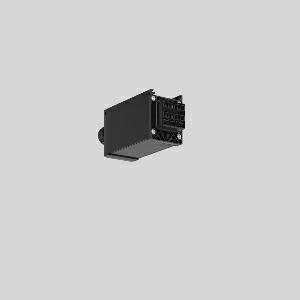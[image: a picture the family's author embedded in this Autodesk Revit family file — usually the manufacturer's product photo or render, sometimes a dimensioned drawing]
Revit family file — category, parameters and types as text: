
# Revit family: linedo_anfangseinspeisung_982859_003_1_55de
name_source: partatom
category: Lighting Fixtures
units: mm (PartAtom-declared; Revit-internal decimal feet)

## family parameters
Cut with Voids When Loaded = No
Host = Face
Light Source = No
Part Type = Normal
Room Calculation Point = No
Round Connector Dimension = Use Diameter
Shared = No

## types (1)
- LINEDO Anfangseinspeisung
    Apparent Load = 0 VA
    Default Elevation = 1800 mm
    Description = Series: LINEDO
Initial power feed (short Version), 7-pole, connection plug. Housing: extruded aluminium profile, powder-coated. Cover made of plastic, surface like housing. LINEDO plug system, plastic, black. 1 cable gland (M25). Cable gland on side or on top. Convenient connection with flat connector.
Colour: black
Length: 152 mm
Width: 58 mm
Height: 76 mm
Weight: 283 g
    Height = 76 mm
    Lamp = 0 x
    Length = 152 mm
    Luminous efficacy = 0 lm/W
    Manufacturer = RZB
    ModVariant = No
    Model = 982859.003.1
    Mounting Place = Ceiling
    Mounting Type = Surface mounted
    Number of Poles = 1
    OnlyDefault = Yes
    Power Factor = 1
    Product Name = LINEDO Anfangseinspeisung
    Product group = Surface mounted continuous line luminaire system
    ProductGroupID = 310
    Protection Class = Protection class I
    Protection Degree = Degree of protection
    RLX_Detail_Level = 1
    RLX_Emergency_Light_Flux = 0 lm
    RLX_Emergency_Type = 0
    RLX_Emergency_Type_DB = No
    RlxData = <blob elided: 14197 chars, md5=03fca468>
    Standby Power = 0 W
    System Light Flux = 0 lm
    System Power = 0 W
    Type Comments = Product without accessories
    Type Image = 982859.003.1.jpg
    URL = http://relux.com
    VarID = ---
    Voltage = 0 V
    Weight = 0.00 kg
    Width = 58 mm

## geometry (parser evidence)
native form markers: Sweep x9
no freeform markers — native parametric forms only
